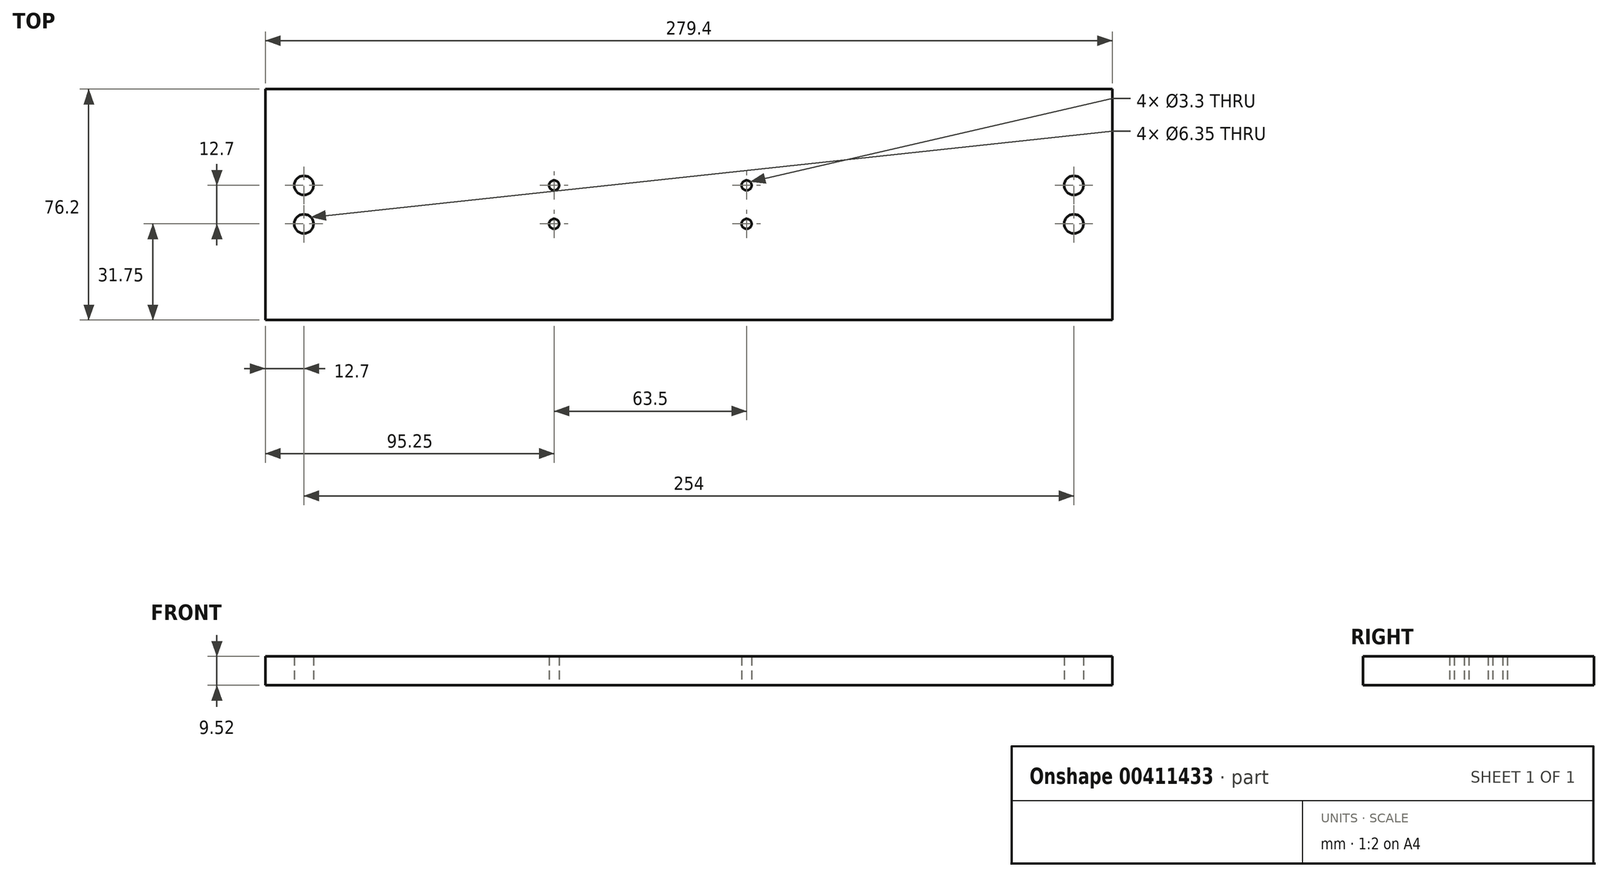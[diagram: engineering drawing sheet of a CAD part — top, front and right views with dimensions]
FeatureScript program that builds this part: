
annotation { "Feature Type Name" : "Feature", "Feature Type Description" : "" }
export const myFeature = defineFeature(function(context is Context, id is Id, definition is map)
    precondition{}
    {
        {
            var Q0;
            Q0=qCreatedBy(makeId("Top.planeOp"),FACE);
            var sketch = newSketch(context, id + "F0", { "sketchPlane" : qUnion([Q0])});
            skLineSegment(sketch, "E0.bottom", {"start": v(-152.4, 31.75) * mm, "end": v(127, 31.75) * mm});
            skLineSegment(sketch, "E0.top", {"start": v(-152.4, -44.45) * mm, "end": v(127, -44.45) * mm});
            skLineSegment(sketch, "E0.left", {"start": v(-152.4, 31.75) * mm, "end": v(-152.4, -44.45) * mm});
            skLineSegment(sketch, "E0.right", {"start": v(127, 31.75) * mm, "end": v(127, -44.45) * mm});
            skLineSegment(sketch, "E1", {"start": v(-163.24, -6.35) * mm, "end": v(141.63, -6.35) * mm});
            skPoint(sketch, "E1.startSnap0", {"position": v(-152.4, -6.35) * mm});
            skCircle(sketch, "E2", {"center": v(-139.7, 0) * mm, "radius": 3.18 * mm});
            skCircle(sketch, "E3", {"center": v(-139.7, -12.7) * mm, "radius": 3.18 * mm});
            skCircle(sketch, "E4", {"center": v(114.3, 0) * mm, "radius": 3.18 * mm});
            skCircle(sketch, "E5", {"center": v(114.3, -12.7) * mm, "radius": 3.18 * mm});
            skLineSegment(sketch, "E6", {"start": v(0, 45.66) * mm, "end": v(0, -77.66) * mm});
            skCircle(sketch, "E7", {"center": v(-57.15, 0) * mm, "radius": 1.65 * mm});
            skCircle(sketch, "E8", {"center": v(-57.15, -12.7) * mm, "radius": 1.65 * mm});
            skCircle(sketch, "E9", {"center": v(6.35, 0) * mm, "radius": 1.65 * mm});
            skCircle(sketch, "E10", {"center": v(6.35, -12.7) * mm, "radius": 1.65 * mm});
            skSolve(sketch);
        }
        {
            var Q0;
            Q0=makeQuery(id+"F0.imprint","IMPRINT",FACE,{"disambiguationData":[TD([[makeQuery(id+"F0.imprint","IMPRINT",EDGE,{"derivedFrom":sQuery(id+"F0.wireOp",EDGE,"E2")}),-1.0]])]});
            var Q1;
            Q1=makeQuery(id+"F0.imprint","IMPRINT",FACE,{"disambiguationData":[TD([[makeQuery(id+"F0.imprint","IMPRINT",EDGE,{"derivedFrom":sQuery(id+"F0.wireOp",EDGE,"E3")}),-1.0]])]});
            var Q2;
            Q2=makeQuery(id+"F0.imprint","IMPRINT",FACE,{"disambiguationData":[TD([[makeQuery(id+"F0.imprint","IMPRINT",EDGE,{"derivedFrom":sQuery(id+"F0.wireOp",EDGE,"E4")}),-1.0]])]});
            var Q3;
            Q3=makeQuery(id+"F0.imprint","IMPRINT",FACE,{"disambiguationData":[TD([[makeQuery(id+"F0.imprint","IMPRINT",EDGE,{"derivedFrom":sQuery(id+"F0.wireOp",EDGE,"E5")}),-1.0]])]});
            extrude(context, id + "F1", {"entities" : qUnion([Q0, Q1, Q2, Q3]), "endBound" : BoundingType.SYMMETRIC, "depth" : 9.52 * mm});
        }
    });
